# Revit family: Thorn Caelon S30i
name_source: partatom
category: Lighting Fixtures
units: mm (PartAtom-declared; Revit-internal decimal feet)

## family parameters
Cut with Voids When Loaded = No
Host = Face
Light Source = No
Maintain Annotation Orientation = No
Part Type = Normal
Room Calculation Point = No
Round Connector Dimension = Use Diameter
Shared = No

## types (193) — shared parameters
Apparent Load = 20 VA
Assembly Code = Pr_70_70_48_75
Description = Outdoor flood and spotlight luminaires
Export Type to IFC As = IfcLightFixtureType
Has Cowl = No
Has Ground Spike = No
Lamp = LED
Luminaire Height = 210 mm  [stored 0.688976 ft]
Luminaire Length = 160 mm  [stored 0.524934 ft]
Luminaire Width = 149 mm  [stored 0.488845 ft]
Manufacturer = Thorn Lighting
Power Factor = 1
Type Accessory Cowl Black = Thorn CAELON-Accessory-S12i_S20i_S30i : CAELON S COWL/BK
Type Accessory Cowl White = Thorn CAELON-Accessory-S12i_S20i_S30i : CAELON S COWL/WH
Type Accessory Ground Spike Black = Thorn CAELON-Accessory-S12i_S20i_S30i : CAELON S12/20/30 GROUND SPIKE
Type Bracket Black = Thorn-Parts-CAELON-Bracket-S12l : Black
Type Bracket White = Thorn-Parts-CAELON-Bracket-S12l : White
Type Housing Black = Thorn-Parts-CAELON-Housing-S12l : Black
Type Housing White = Thorn-Parts-CAELON-Housing-S12l : White
Type IFC Predefined Type = DIRECTIONSOURCE
URL = https://www.thornlighting.com
zero-valued in all types: Default Elevation

## per-type parameters (varying)
| type | Housing Finish Black | Housing Finish White | Model | Optic | Type Accessory Cowl | Type Bracket | Type Housing | Type Image | Type Light Source |
| CAELON S30i 3000-827 5D WH 66 BC | No | Yes | 21034300 | - | Thorn CAELON-Accessory-S12i_S20i_S30i : CAELON S COWL/WH | Thorn-Parts-CAELON-Bracket-S12l : White | Thorn-Parts-CAELON-Housing-S12l : White | TLG_CAEL_F_S12i-S20i-S30i_WH.png | Thorn-Light Sources-CAELON S30i : CAELON S30i 3000-827 5D WH 66 BC_photometric_data |
| CAELON S30i 3000-827 M BK 66 BC | Yes | No | 21035660 | Medium | Thorn CAELON-Accessory-S12i_S20i_S30i : CAELON S COWL/BK | Thorn-Parts-CAELON-Bracket-S12l : Black | Thorn-Parts-CAELON-Housing-S12l : Black | TLG_CAEL_F_S12i-S20i-S30i_BK.png | Thorn-Light Sources-CAELON S30i : CAELON S30i 3000-827 M BK 66 BC_photometric_data |
| CAELON S30I 3000-827 M BK 66 HF | Yes | No | 21035658 | Medium | Thorn CAELON-Accessory-S12i_S20i_S30i : CAELON S COWL/BK | Thorn-Parts-CAELON-Bracket-S12l : Black | Thorn-Parts-CAELON-Housing-S12l : Black | TLG_CAEL_F_S12i-S20i-S30i_BK.png | Thorn-Light Sources-CAELON S30i : CAELON S30I 3000-827 M BK 66 HF_photometric_data |
| CAELON S30I 3000-827 M BK 66 HFX | Yes | No | 21035659 | Medium | Thorn CAELON-Accessory-S12i_S20i_S30i : CAELON S COWL/BK | Thorn-Parts-CAELON-Bracket-S12l : Black | Thorn-Parts-CAELON-Housing-S12l : Black | TLG_CAEL_F_S12i-S20i-S30i_BK.png | Thorn-Light Sources-CAELON S30i : CAELON S30I 3000-827 M BK 66 HFX_photometric_data |
| CAELON S30i 3000-827 M BK HL 66 BC | Yes | No | 21035657 | Medium | Thorn CAELON-Accessory-S12i_S20i_S30i : CAELON S COWL/BK | Thorn-Parts-CAELON-Bracket-S12l : Black | Thorn-Parts-CAELON-Housing-S12l : Black | TLG_CAEL_F_S12i-S20i-S30i_BK.png | Thorn-Light Sources-CAELON S30i : CAELON S30i 3000-827 M BK HL 66 BC_photometric_data |
| CAELON S30I 3000-827 M BK HL 66 HF | Yes | No | 21035655 | Medium | Thorn CAELON-Accessory-S12i_S20i_S30i : CAELON S COWL/BK | Thorn-Parts-CAELON-Bracket-S12l : Black | Thorn-Parts-CAELON-Housing-S12l : Black | TLG_CAEL_F_S12i-S20i-S30i_BK.png | Thorn-Light Sources-CAELON S30i : CAELON S30I 3000-827 M BK HL 66 HF_photometric_data |
| CAELON S30I 3000-827 M BK HL 66 HFX | Yes | No | 21035656 | Medium | Thorn CAELON-Accessory-S12i_S20i_S30i : CAELON S COWL/BK | Thorn-Parts-CAELON-Bracket-S12l : Black | Thorn-Parts-CAELON-Housing-S12l : Black | TLG_CAEL_F_S12i-S20i-S30i_BK.png | Thorn-Light Sources-CAELON S30i : CAELON S30I 3000-827 M BK HL 66 HFX_photometric_data |
| CAELON S30i 3000-827 M WH 66 BC | No | Yes | 21035666 | Medium | Thorn CAELON-Accessory-S12i_S20i_S30i : CAELON S COWL/WH | Thorn-Parts-CAELON-Bracket-S12l : White | Thorn-Parts-CAELON-Housing-S12l : White | TLG_CAEL_F_S12i-S20i-S30i_WH.png | Thorn-Light Sources-CAELON S30i : CAELON S30i 3000-827 M WH 66 BC_photometric_data |
| CAELON S30I 3000-827 M WH 66 HF | No | Yes | 21035664 | Medium | Thorn CAELON-Accessory-S12i_S20i_S30i : CAELON S COWL/WH | Thorn-Parts-CAELON-Bracket-S12l : White | Thorn-Parts-CAELON-Housing-S12l : White | TLG_CAEL_F_S12i-S20i-S30i_WH.png | Thorn-Light Sources-CAELON S30i : CAELON S30I 3000-827 M WH 66 HF_photometric_data |
| CAELON S30I 3000-827 M WH 66 HFX | No | Yes | 21035665 | Medium | Thorn CAELON-Accessory-S12i_S20i_S30i : CAELON S COWL/WH | Thorn-Parts-CAELON-Bracket-S12l : White | Thorn-Parts-CAELON-Housing-S12l : White | TLG_CAEL_F_S12i-S20i-S30i_WH.png | Thorn-Light Sources-CAELON S30i : CAELON S30I 3000-827 M WH 66 HFX_photometric_data |
| CAELON S30i 3000-827 M WH HL 66 BC | No | Yes | 21035663 | Medium | Thorn CAELON-Accessory-S12i_S20i_S30i : CAELON S COWL/WH | Thorn-Parts-CAELON-Bracket-S12l : White | Thorn-Parts-CAELON-Housing-S12l : White | TLG_CAEL_F_S12i-S20i-S30i_WH.png | Thorn-Light Sources-CAELON S30i : CAELON S30i 3000-827 M WH HL 66 BC_photometric_data |
| CAELON S30I 3000-827 M WH HL 66 HF | No | Yes | 21035661 | Medium | Thorn CAELON-Accessory-S12i_S20i_S30i : CAELON S COWL/WH | Thorn-Parts-CAELON-Bracket-S12l : White | Thorn-Parts-CAELON-Housing-S12l : White | TLG_CAEL_F_S12i-S20i-S30i_WH.png | Thorn-Light Sources-CAELON S30i : CAELON S30I 3000-827 M WH HL 66 HF_photometric_data |
| CAELON S30I 3000-827 M WH HL 66 HFX | No | Yes | 21035662 | Medium | Thorn CAELON-Accessory-S12i_S20i_S30i : CAELON S COWL/WH | Thorn-Parts-CAELON-Bracket-S12l : White | Thorn-Parts-CAELON-Housing-S12l : White | TLG_CAEL_F_S12i-S20i-S30i_WH.png | Thorn-Light Sources-CAELON S30i : CAELON S30I 3000-827 M WH HL 66 HFX_photometric_data |
| CAELON S30i 3000-827 N BK 66 BC | Yes | No | 21034286 | Narrow | Thorn CAELON-Accessory-S12i_S20i_S30i : CAELON S COWL/BK | Thorn-Parts-CAELON-Bracket-S12l : Black | Thorn-Parts-CAELON-Housing-S12l : Black | TLG_CAEL_F_S12i-S20i-S30i_BK.png | Thorn-Light Sources-CAELON S30i : CAELON S30i 3000-827 N BK 66 BC_photometric_data |
| CAELON S30I 3000-827 N BK 66 HF | Yes | No | 21034284 | Narrow | Thorn CAELON-Accessory-S12i_S20i_S30i : CAELON S COWL/BK | Thorn-Parts-CAELON-Bracket-S12l : Black | Thorn-Parts-CAELON-Housing-S12l : Black | TLG_CAEL_F_S12i-S20i-S30i_BK.png | Thorn-Light Sources-CAELON S30i : CAELON S30I 3000-827 N BK 66 HF_photometric_data |
| CAELON S30I 3000-827 N BK 66 HFX | Yes | No | 21034285 | Narrow | Thorn CAELON-Accessory-S12i_S20i_S30i : CAELON S COWL/BK | Thorn-Parts-CAELON-Bracket-S12l : Black | Thorn-Parts-CAELON-Housing-S12l : Black | TLG_CAEL_F_S12i-S20i-S30i_BK.png | Thorn-Light Sources-CAELON S30i : CAELON S30I 3000-827 N BK 66 HFX_photometric_data |
| CAELON S30i 3000-827 N BK HL 66 BC | Yes | No | 21034283 | Narrow | Thorn CAELON-Accessory-S12i_S20i_S30i : CAELON S COWL/BK | Thorn-Parts-CAELON-Bracket-S12l : Black | Thorn-Parts-CAELON-Housing-S12l : Black | TLG_CAEL_F_S12i-S20i-S30i_BK.png | Thorn-Light Sources-CAELON S30i : CAELON S30i 3000-827 N BK HL 66 BC_photometric_data |
| CAELON S30I 3000-827 N BK HL 66 HF | Yes | No | 21034281 | Narrow | Thorn CAELON-Accessory-S12i_S20i_S30i : CAELON S COWL/BK | Thorn-Parts-CAELON-Bracket-S12l : Black | Thorn-Parts-CAELON-Housing-S12l : Black | TLG_CAEL_F_S12i-S20i-S30i_BK.png | Thorn-Light Sources-CAELON S30i : CAELON S30I 3000-827 N BK HL 66 HF_photometric_data |
| CAELON S30I 3000-827 N BK HL 66 HFX | Yes | No | 21034282 | Narrow | Thorn CAELON-Accessory-S12i_S20i_S30i : CAELON S COWL/BK | Thorn-Parts-CAELON-Bracket-S12l : Black | Thorn-Parts-CAELON-Housing-S12l : Black | TLG_CAEL_F_S12i-S20i-S30i_BK.png | Thorn-Light Sources-CAELON S30i : CAELON S30I 3000-827 N BK HL 66 HFX_photometric_data |
| CAELON S30i 3000-827 N WH 66 BC | No | Yes | 21034292 | Narrow | Thorn CAELON-Accessory-S12i_S20i_S30i : CAELON S COWL/WH | Thorn-Parts-CAELON-Bracket-S12l : White | Thorn-Parts-CAELON-Housing-S12l : White | TLG_CAEL_F_S12i-S20i-S30i_WH.png | Thorn-Light Sources-CAELON S30i : CAELON S30i 3000-827 N WH 66 BC_photometric_data |
| CAELON S30I 3000-827 N WH 66 HF | No | Yes | 21034290 | Narrow | Thorn CAELON-Accessory-S12i_S20i_S30i : CAELON S COWL/WH | Thorn-Parts-CAELON-Bracket-S12l : White | Thorn-Parts-CAELON-Housing-S12l : White | TLG_CAEL_F_S12i-S20i-S30i_WH.png | Thorn-Light Sources-CAELON S30i : CAELON S30I 3000-827 N WH 66 HF_photometric_data |
| CAELON S30I 3000-827 N WH 66 HFX | No | Yes | 21034291 | Narrow | Thorn CAELON-Accessory-S12i_S20i_S30i : CAELON S COWL/WH | Thorn-Parts-CAELON-Bracket-S12l : White | Thorn-Parts-CAELON-Housing-S12l : White | TLG_CAEL_F_S12i-S20i-S30i_WH.png | Thorn-Light Sources-CAELON S30i : CAELON S30I 3000-827 N WH 66 HFX_photometric_data |
| CAELON S30i 3000-827 N WH HL 66 BC | No | Yes | 21034289 | Narrow | Thorn CAELON-Accessory-S12i_S20i_S30i : CAELON S COWL/WH | Thorn-Parts-CAELON-Bracket-S12l : White | Thorn-Parts-CAELON-Housing-S12l : White | TLG_CAEL_F_S12i-S20i-S30i_WH.png | Thorn-Light Sources-CAELON S30i : CAELON S30i 3000-827 N WH HL 66 BC_photometric_data |
| CAELON S30I 3000-827 N WH HL 66 HF | No | Yes | 21034287 | Narrow | Thorn CAELON-Accessory-S12i_S20i_S30i : CAELON S COWL/WH | Thorn-Parts-CAELON-Bracket-S12l : White | Thorn-Parts-CAELON-Housing-S12l : White | TLG_CAEL_F_S12i-S20i-S30i_WH.png | Thorn-Light Sources-CAELON S30i : CAELON S30I 3000-827 N WH HL 66 HF_photometric_data |
| CAELON S30I 3000-827 N WH HL 66 HFX | No | Yes | 21034288 | Narrow | Thorn CAELON-Accessory-S12i_S20i_S30i : CAELON S COWL/WH | Thorn-Parts-CAELON-Bracket-S12l : White | Thorn-Parts-CAELON-Housing-S12l : White | TLG_CAEL_F_S12i-S20i-S30i_WH.png | Thorn-Light Sources-CAELON S30i : CAELON S30I 3000-827 N WH HL 66 HFX_photometric_data |
| CAELON S30i 3000-827 SN BK 66 BC | Yes | No | 21034274 | Super Narrow | Thorn CAELON-Accessory-S12i_S20i_S30i : CAELON S COWL/BK | Thorn-Parts-CAELON-Bracket-S12l : Black | Thorn-Parts-CAELON-Housing-S12l : Black | TLG_CAEL_F_S12i-S20i-S30i_BK.png | Thorn-Light Sources-CAELON S30i : CAELON S30i 3000-827 SN BK 66 BC_photometric_data |
| CAELON S30I 3000-827 SN BK 66 HF | Yes | No | 21034272 | Super Narrow | Thorn CAELON-Accessory-S12i_S20i_S30i : CAELON S COWL/BK | Thorn-Parts-CAELON-Bracket-S12l : Black | Thorn-Parts-CAELON-Housing-S12l : Black | TLG_CAEL_F_S12i-S20i-S30i_BK.png | Thorn-Light Sources-CAELON S30i : CAELON S30I 3000-827 SN BK 66 HF_photometric_data |
| CAELON S30I 3000-827 SN BK 66 HFX | Yes | No | 21034273 | Super Narrow | Thorn CAELON-Accessory-S12i_S20i_S30i : CAELON S COWL/BK | Thorn-Parts-CAELON-Bracket-S12l : Black | Thorn-Parts-CAELON-Housing-S12l : Black | TLG_CAEL_F_S12i-S20i-S30i_BK.png | Thorn-Light Sources-CAELON S30i : CAELON S30I 3000-827 SN BK 66 HFX_photometric_data |
| CAELON S30i 3000-827 SN BK HL 66 BC | Yes | No | 21034271 | Super Narrow | Thorn CAELON-Accessory-S12i_S20i_S30i : CAELON S COWL/BK | Thorn-Parts-CAELON-Bracket-S12l : Black | Thorn-Parts-CAELON-Housing-S12l : Black | TLG_CAEL_F_S12i-S20i-S30i_BK.png | Thorn-Light Sources-CAELON S30i : CAELON S30i 3000-827 SN BK HL 66 BC_photometric_data |
| CAELON S30I 3000-827 SN BK HL 66 HF | Yes | No | 21034269 | Super Narrow | Thorn CAELON-Accessory-S12i_S20i_S30i : CAELON S COWL/BK | Thorn-Parts-CAELON-Bracket-S12l : Black | Thorn-Parts-CAELON-Housing-S12l : Black | TLG_CAEL_F_S12i-S20i-S30i_BK.png | Thorn-Light Sources-CAELON S30i : CAELON S30I 3000-827 SN BK HL 66 HF_photometric_data |
| CAELON S30I 3000-827 SN BK HL 66 HFX | Yes | No | 21034270 | Super Narrow | Thorn CAELON-Accessory-S12i_S20i_S30i : CAELON S COWL/BK | Thorn-Parts-CAELON-Bracket-S12l : Black | Thorn-Parts-CAELON-Housing-S12l : Black | TLG_CAEL_F_S12i-S20i-S30i_BK.png | Thorn-Light Sources-CAELON S30i : CAELON S30I 3000-827 SN BK HL 66 HFX_photometric_data |
| CAELON S30i 3000-827 SN WH 66 BC | No | Yes | 21034280 | Super Narrow | Thorn CAELON-Accessory-S12i_S20i_S30i : CAELON S COWL/WH | Thorn-Parts-CAELON-Bracket-S12l : White | Thorn-Parts-CAELON-Housing-S12l : White | TLG_CAEL_F_S12i-S20i-S30i_WH.png | Thorn-Light Sources-CAELON S30i : CAELON S30i 3000-827 SN WH 66 BC_photometric_data |
| CAELON S30I 3000-827 SN WH 66 HF | No | Yes | 21034278 | Super Narrow | Thorn CAELON-Accessory-S12i_S20i_S30i : CAELON S COWL/WH | Thorn-Parts-CAELON-Bracket-S12l : White | Thorn-Parts-CAELON-Housing-S12l : White | TLG_CAEL_F_S12i-S20i-S30i_WH.png | Thorn-Light Sources-CAELON S30i : CAELON S30I 3000-827 SN WH 66 HF_photometric_data |
| CAELON S30I 3000-827 SN WH 66 HFX | No | Yes | 21034279 | Super Narrow | Thorn CAELON-Accessory-S12i_S20i_S30i : CAELON S COWL/WH | Thorn-Parts-CAELON-Bracket-S12l : White | Thorn-Parts-CAELON-Housing-S12l : White | TLG_CAEL_F_S12i-S20i-S30i_WH.png | Thorn-Light Sources-CAELON S30i : CAELON S30I 3000-827 SN WH 66 HFX_photometric_data |
| CAELON S30i 3000-827 SN WH HL 66 BC | No | Yes | 21034277 | Super Narrow | Thorn CAELON-Accessory-S12i_S20i_S30i : CAELON S COWL/WH | Thorn-Parts-CAELON-Bracket-S12l : White | Thorn-Parts-CAELON-Housing-S12l : White | TLG_CAEL_F_S12i-S20i-S30i_WH.png | Thorn-Light Sources-CAELON S30i : CAELON S30i 3000-827 SN WH HL 66 BC_photometric_data |
| CAELON S30I 3000-827 SN WH HL 66 HF | No | Yes | 21034275 | Super Narrow | Thorn CAELON-Accessory-S12i_S20i_S30i : CAELON S COWL/WH | Thorn-Parts-CAELON-Bracket-S12l : White | Thorn-Parts-CAELON-Housing-S12l : White | TLG_CAEL_F_S12i-S20i-S30i_WH.png | Thorn-Light Sources-CAELON S30i : CAELON S30I 3000-827 SN WH HL 66 HF_photometric_data |
| CAELON S30I 3000-827 SN WH HL 66 HFX | No | Yes | 21034276 | Super Narrow | Thorn CAELON-Accessory-S12i_S20i_S30i : CAELON S COWL/WH | Thorn-Parts-CAELON-Bracket-S12l : White | Thorn-Parts-CAELON-Housing-S12l : White | TLG_CAEL_F_S12i-S20i-S30i_WH.png | Thorn-Light Sources-CAELON S30i : CAELON S30I 3000-827 SN WH HL 66 HFX_photometric_data |
| CAELON S30i 3000-827 W BK 66 BC | Yes | No | 21034295 | Wide | Thorn CAELON-Accessory-S12i_S20i_S30i : CAELON S COWL/BK | Thorn-Parts-CAELON-Bracket-S12l : Black | Thorn-Parts-CAELON-Housing-S12l : Black | TLG_CAEL_F_S12i-S20i-S30i_BK.png | Thorn-Light Sources-CAELON S30i : CAELON S30i 3000-827 W BK 66 BC_photometric_data |
| CAELON S30I 3000-827 W BK 66 HF | Yes | No | 21034293 | Wide | Thorn CAELON-Accessory-S12i_S20i_S30i : CAELON S COWL/BK | Thorn-Parts-CAELON-Bracket-S12l : Black | Thorn-Parts-CAELON-Housing-S12l : Black | TLG_CAEL_F_S12i-S20i-S30i_BK.png | Thorn-Light Sources-CAELON S30i : CAELON S30I 3000-827 W BK 66 HF_photometric_data |
| CAELON S30I 3000-827 W BK 66 HFX | Yes | No | 21034294 | Wide | Thorn CAELON-Accessory-S12i_S20i_S30i : CAELON S COWL/BK | Thorn-Parts-CAELON-Bracket-S12l : Black | Thorn-Parts-CAELON-Housing-S12l : Black | TLG_CAEL_F_S12i-S20i-S30i_BK.png | Thorn-Light Sources-CAELON S30i : CAELON S30I 3000-827 W BK 66 HFX_photometric_data |
| CAELON S30i 3000-827 W WH 66 BC | No | Yes | 21034298 | Wide | Thorn CAELON-Accessory-S12i_S20i_S30i : CAELON S COWL/WH | Thorn-Parts-CAELON-Bracket-S12l : White | Thorn-Parts-CAELON-Housing-S12l : White | TLG_CAEL_F_S12i-S20i-S30i_WH.png | Thorn-Light Sources-CAELON S30i : CAELON S30i 3000-827 W WH 66 BC_photometric_data |
| CAELON S30I 3000-827 W WH 66 HF | No | Yes | 21034296 | Wide | Thorn CAELON-Accessory-S12i_S20i_S30i : CAELON S COWL/WH | Thorn-Parts-CAELON-Bracket-S12l : White | Thorn-Parts-CAELON-Housing-S12l : White | TLG_CAEL_F_S12i-S20i-S30i_WH.png | Thorn-Light Sources-CAELON S30i : CAELON S30I 3000-827 W WH 66 HF_photometric_data |
| CAELON S30I 3000-827 W WH 66 HFX | No | Yes | 21034297 | Wide | Thorn CAELON-Accessory-S12i_S20i_S30i : CAELON S COWL/WH | Thorn-Parts-CAELON-Bracket-S12l : White | Thorn-Parts-CAELON-Housing-S12l : White | TLG_CAEL_F_S12i-S20i-S30i_WH.png | Thorn-Light Sources-CAELON S30i : CAELON S30I 3000-827 W WH 66 HFX_photometric_data |
| CAELON S30i 3000-830 5D BK 66 BC | Yes | No | 21034331 |  | Thorn CAELON-Accessory-S12i_S20i_S30i : CAELON S COWL/BK | Thorn-Parts-CAELON-Bracket-S12l : Black | Thorn-Parts-CAELON-Housing-S12l : Black | TLG_CAEL_F_S12i-S20i-S30i_BK.png | Thorn-Light Sources-CAELON S30i : CAELON S30i 3000-830 5D BK 66 BC_photometric_data |
| CAELON S30i 3000-830 5D WH 66 BC | No | Yes | 21034332 |  | Thorn CAELON-Accessory-S12i_S20i_S30i : CAELON S COWL/WH | Thorn-Parts-CAELON-Bracket-S12l : White | Thorn-Parts-CAELON-Housing-S12l : White | TLG_CAEL_F_S12i-S20i-S30i_WH.png | Thorn-Light Sources-CAELON S30i : CAELON S30i 3000-830 5D WH 66 BC_photometric_data |
| CAELON S30i 3000-830 M BK 66 BC | Yes | No | 21035672 | Medium | Thorn CAELON-Accessory-S12i_S20i_S30i : CAELON S COWL/BK | Thorn-Parts-CAELON-Bracket-S12l : Black | Thorn-Parts-CAELON-Housing-S12l : Black | TLG_CAEL_F_S12i-S20i-S30i_BK.png | Thorn-Light Sources-CAELON S30i : CAELON S30i 3000-830 M BK 66 BC_photometric_data |
| CAELON S30I 3000-830 M BK 66 HF | Yes | No | 21035670 | Medium | Thorn CAELON-Accessory-S12i_S20i_S30i : CAELON S COWL/BK | Thorn-Parts-CAELON-Bracket-S12l : Black | Thorn-Parts-CAELON-Housing-S12l : Black | TLG_CAEL_F_S12i-S20i-S30i_BK.png | Thorn-Light Sources-CAELON S30i : CAELON S30I 3000-830 M BK 66 HF_photometric_data |
| CAELON S30I 3000-830 M BK 66 HFX | Yes | No | 21035671 | Medium | Thorn CAELON-Accessory-S12i_S20i_S30i : CAELON S COWL/BK | Thorn-Parts-CAELON-Bracket-S12l : Black | Thorn-Parts-CAELON-Housing-S12l : Black | TLG_CAEL_F_S12i-S20i-S30i_BK.png | Thorn-Light Sources-CAELON S30i : CAELON S30I 3000-830 M BK 66 HFX_photometric_data |
| CAELON S30i 3000-830 M BK HL 66 BC | Yes | No | 21035669 | Medium | Thorn CAELON-Accessory-S12i_S20i_S30i : CAELON S COWL/BK | Thorn-Parts-CAELON-Bracket-S12l : Black | Thorn-Parts-CAELON-Housing-S12l : Black | TLG_CAEL_F_S12i-S20i-S30i_BK.png | Thorn-Light Sources-CAELON S30i : CAELON S30i 3000-830 M BK HL 66 BC_photometric_data |
| CAELON S30I 3000-830 M BK HL 66 HF | Yes | No | 21035667 | Medium | Thorn CAELON-Accessory-S12i_S20i_S30i : CAELON S COWL/BK | Thorn-Parts-CAELON-Bracket-S12l : Black | Thorn-Parts-CAELON-Housing-S12l : Black | TLG_CAEL_F_S12i-S20i-S30i_BK.png | Thorn-Light Sources-CAELON S30i : CAELON S30I 3000-830 M BK HL 66 HF_photometric_data |
| CAELON S30I 3000-830 M BK HL 66 HFX | Yes | No | 21035668 | Medium | Thorn CAELON-Accessory-S12i_S20i_S30i : CAELON S COWL/BK | Thorn-Parts-CAELON-Bracket-S12l : Black | Thorn-Parts-CAELON-Housing-S12l : Black | TLG_CAEL_F_S12i-S20i-S30i_BK.png | Thorn-Light Sources-CAELON S30i : CAELON S30I 3000-830 M BK HL 66 HFX_photometric_data |
| CAELON S30i 3000-830 M WH 66 BC | No | Yes | 21035678 | Medium | Thorn CAELON-Accessory-S12i_S20i_S30i : CAELON S COWL/WH | Thorn-Parts-CAELON-Bracket-S12l : White | Thorn-Parts-CAELON-Housing-S12l : White | TLG_CAEL_F_S12i-S20i-S30i_WH.png | Thorn-Light Sources-CAELON S30i : CAELON S30i 3000-830 M WH 66 BC_photometric_data |
| CAELON S30I 3000-830 M WH 66 HF | No | Yes | 21035676 | Medium | Thorn CAELON-Accessory-S12i_S20i_S30i : CAELON S COWL/WH | Thorn-Parts-CAELON-Bracket-S12l : White | Thorn-Parts-CAELON-Housing-S12l : White | TLG_CAEL_F_S12i-S20i-S30i_WH.png | Thorn-Light Sources-CAELON S30i : CAELON S30I 3000-830 M WH 66 HF_photometric_data |
| CAELON S30I 3000-830 M WH 66 HFX | No | Yes | 21035677 | Medium | Thorn CAELON-Accessory-S12i_S20i_S30i : CAELON S COWL/WH | Thorn-Parts-CAELON-Bracket-S12l : White | Thorn-Parts-CAELON-Housing-S12l : White | TLG_CAEL_F_S12i-S20i-S30i_WH.png | Thorn-Light Sources-CAELON S30i : CAELON S30I 3000-830 M WH 66 HFX_photometric_data |
| CAELON S30i 3000-830 M WH HL 66 BC | No | Yes | 21035675 | Medium | Thorn CAELON-Accessory-S12i_S20i_S30i : CAELON S COWL/WH | Thorn-Parts-CAELON-Bracket-S12l : White | Thorn-Parts-CAELON-Housing-S12l : White | TLG_CAEL_F_S12i-S20i-S30i_WH.png | Thorn-Light Sources-CAELON S30i : CAELON S30i 3000-830 M WH HL 66 BC_photometric_data |
| CAELON S30I 3000-830 M WH HL 66 HF | No | Yes | 21035673 | Medium | Thorn CAELON-Accessory-S12i_S20i_S30i : CAELON S COWL/WH | Thorn-Parts-CAELON-Bracket-S12l : White | Thorn-Parts-CAELON-Housing-S12l : White | TLG_CAEL_F_S12i-S20i-S30i_WH.png | Thorn-Light Sources-CAELON S30i : CAELON S30I 3000-830 M WH HL 66 HF_photometric_data |
| CAELON S30I 3000-830 M WH HL 66 HFX | No | Yes | 21035674 | Medium | Thorn CAELON-Accessory-S12i_S20i_S30i : CAELON S COWL/WH | Thorn-Parts-CAELON-Bracket-S12l : White | Thorn-Parts-CAELON-Housing-S12l : White | TLG_CAEL_F_S12i-S20i-S30i_WH.png | Thorn-Light Sources-CAELON S30i : CAELON S30I 3000-830 M WH HL 66 HFX_photometric_data |
| CAELON S30i 3000-830 N BK 66 BC | Yes | No | 21034318 | Narrow | Thorn CAELON-Accessory-S12i_S20i_S30i : CAELON S COWL/BK | Thorn-Parts-CAELON-Bracket-S12l : Black | Thorn-Parts-CAELON-Housing-S12l : Black | TLG_CAEL_F_S12i-S20i-S30i_BK.png | Thorn-Light Sources-CAELON S30i : CAELON S30i 3000-830 N BK 66 BC_photometric_data |
| CAELON S30I 3000-830 N BK 66 HF | Yes | No | 21034316 | Narrow | Thorn CAELON-Accessory-S12i_S20i_S30i : CAELON S COWL/BK | Thorn-Parts-CAELON-Bracket-S12l : Black | Thorn-Parts-CAELON-Housing-S12l : Black | TLG_CAEL_F_S12i-S20i-S30i_BK.png | Thorn-Light Sources-CAELON S30i : CAELON S30I 3000-830 N BK 66 HF_photometric_data |
| CAELON S30I 3000-830 N BK 66 HFX | Yes | No | 21034317 | Narrow | Thorn CAELON-Accessory-S12i_S20i_S30i : CAELON S COWL/BK | Thorn-Parts-CAELON-Bracket-S12l : Black | Thorn-Parts-CAELON-Housing-S12l : Black | TLG_CAEL_F_S12i-S20i-S30i_BK.png | Thorn-Light Sources-CAELON S30i : CAELON S30I 3000-830 N BK 66 HFX_photometric_data |
| CAELON S30i 3000-830 N BK HL 66 BC | Yes | No | 21034315 | Narrow | Thorn CAELON-Accessory-S12i_S20i_S30i : CAELON S COWL/BK | Thorn-Parts-CAELON-Bracket-S12l : Black | Thorn-Parts-CAELON-Housing-S12l : Black | TLG_CAEL_F_S12i-S20i-S30i_BK.png | Thorn-Light Sources-CAELON S30i : CAELON S30i 3000-830 N BK HL 66 BC_photometric_data |
| CAELON S30I 3000-830 N BK HL 66 HF | Yes | No | 21034313 | Narrow | Thorn CAELON-Accessory-S12i_S20i_S30i : CAELON S COWL/BK | Thorn-Parts-CAELON-Bracket-S12l : Black | Thorn-Parts-CAELON-Housing-S12l : Black | TLG_CAEL_F_S12i-S20i-S30i_BK.png | Thorn-Light Sources-CAELON S30i : CAELON S30I 3000-830 N BK HL 66 HF_photometric_data |
| CAELON S30I 3000-830 N BK HL 66 HFX | Yes | No | 21034314 | Narrow | Thorn CAELON-Accessory-S12i_S20i_S30i : CAELON S COWL/BK | Thorn-Parts-CAELON-Bracket-S12l : Black | Thorn-Parts-CAELON-Housing-S12l : Black | TLG_CAEL_F_S12i-S20i-S30i_BK.png | Thorn-Light Sources-CAELON S30i : CAELON S30I 3000-830 N BK HL 66 HFX_photometric_data |
| CAELON S30i 3000-830 N WH 66 BC | No | Yes | 21034324 | Narrow | Thorn CAELON-Accessory-S12i_S20i_S30i : CAELON S COWL/WH | Thorn-Parts-CAELON-Bracket-S12l : White | Thorn-Parts-CAELON-Housing-S12l : White | TLG_CAEL_F_S12i-S20i-S30i_WH.png | Thorn-Light Sources-CAELON S30i : CAELON S30i 3000-830 N WH 66 BC_photometric_data |
| CAELON S30I 3000-830 N WH 66 HF | No | Yes | 21034322 | Narrow | Thorn CAELON-Accessory-S12i_S20i_S30i : CAELON S COWL/WH | Thorn-Parts-CAELON-Bracket-S12l : White | Thorn-Parts-CAELON-Housing-S12l : White | TLG_CAEL_F_S12i-S20i-S30i_WH.png | Thorn-Light Sources-CAELON S30i : CAELON S30I 3000-830 N WH 66 HF_photometric_data |
| CAELON S30I 3000-830 N WH 66 HFX | No | Yes | 21034323 | Narrow | Thorn CAELON-Accessory-S12i_S20i_S30i : CAELON S COWL/WH | Thorn-Parts-CAELON-Bracket-S12l : White | Thorn-Parts-CAELON-Housing-S12l : White | TLG_CAEL_F_S12i-S20i-S30i_WH.png | Thorn-Light Sources-CAELON S30i : CAELON S30I 3000-830 N WH 66 HFX_photometric_data |
| CAELON S30i 3000-830 N WH HL 66 BC | No | Yes | 21034321 | Narrow | Thorn CAELON-Accessory-S12i_S20i_S30i : CAELON S COWL/WH | Thorn-Parts-CAELON-Bracket-S12l : White | Thorn-Parts-CAELON-Housing-S12l : White | TLG_CAEL_F_S12i-S20i-S30i_WH.png | Thorn-Light Sources-CAELON S30i : CAELON S30i 3000-830 N WH HL 66 BC_photometric_data |
| CAELON S30I 3000-830 N WH HL 66 HF | No | Yes | 21034319 | Narrow | Thorn CAELON-Accessory-S12i_S20i_S30i : CAELON S COWL/WH | Thorn-Parts-CAELON-Bracket-S12l : White | Thorn-Parts-CAELON-Housing-S12l : White | TLG_CAEL_F_S12i-S20i-S30i_WH.png | Thorn-Light Sources-CAELON S30i : CAELON S30I 3000-830 N WH HL 66 HF_photometric_data |
| CAELON S30I 3000-830 N WH HL 66 HFX | No | Yes | 21034320 | Narrow | Thorn CAELON-Accessory-S12i_S20i_S30i : CAELON S COWL/WH | Thorn-Parts-CAELON-Bracket-S12l : White | Thorn-Parts-CAELON-Housing-S12l : White | TLG_CAEL_F_S12i-S20i-S30i_WH.png | Thorn-Light Sources-CAELON S30i : CAELON S30I 3000-830 N WH HL 66 HFX_photometric_data |
| CAELON S30i 3000-830 SN BK 66 BC | Yes | No | 21034306 | Super Narrow | Thorn CAELON-Accessory-S12i_S20i_S30i : CAELON S COWL/BK | Thorn-Parts-CAELON-Bracket-S12l : Black | Thorn-Parts-CAELON-Housing-S12l : Black | TLG_CAEL_F_S12i-S20i-S30i_BK.png | Thorn-Light Sources-CAELON S30i : CAELON S30i 3000-830 SN BK 66 BC_photometric_data |
| CAELON S30I 3000-830 SN BK 66 HF | Yes | No | 21034304 | Super Narrow | Thorn CAELON-Accessory-S12i_S20i_S30i : CAELON S COWL/BK | Thorn-Parts-CAELON-Bracket-S12l : Black | Thorn-Parts-CAELON-Housing-S12l : Black | TLG_CAEL_F_S12i-S20i-S30i_BK.png | Thorn-Light Sources-CAELON S30i : CAELON S30I 3000-830 SN BK 66 HF_photometric_data |
| CAELON S30I 3000-830 SN BK 66 HFX | Yes | No | 21034305 | Super Narrow | Thorn CAELON-Accessory-S12i_S20i_S30i : CAELON S COWL/BK | Thorn-Parts-CAELON-Bracket-S12l : Black | Thorn-Parts-CAELON-Housing-S12l : Black | TLG_CAEL_F_S12i-S20i-S30i_BK.png | Thorn-Light Sources-CAELON S30i : CAELON S30I 3000-830 SN BK 66 HFX_photometric_data |
| CAELON S30i 3000-830 SN BK HL 66 BC | Yes | No | 21034303 | Super Narrow | Thorn CAELON-Accessory-S12i_S20i_S30i : CAELON S COWL/BK | Thorn-Parts-CAELON-Bracket-S12l : Black | Thorn-Parts-CAELON-Housing-S12l : Black | TLG_CAEL_F_S12i-S20i-S30i_BK.png | Thorn-Light Sources-CAELON S30i : CAELON S30i 3000-830 SN BK HL 66 BC_photometric_data |
| CAELON S30I 3000-830 SN BK HL 66 HF | Yes | No | 21034301 | Super Narrow | Thorn CAELON-Accessory-S12i_S20i_S30i : CAELON S COWL/BK | Thorn-Parts-CAELON-Bracket-S12l : Black | Thorn-Parts-CAELON-Housing-S12l : Black | TLG_CAEL_F_S12i-S20i-S30i_BK.png | Thorn-Light Sources-CAELON S30i : CAELON S30I 3000-830 SN BK HL 66 HF_photometric_data |
| CAELON S30I 3000-830 SN BK HL 66 HFX | Yes | No | 21034302 | Super Narrow | Thorn CAELON-Accessory-S12i_S20i_S30i : CAELON S COWL/BK | Thorn-Parts-CAELON-Bracket-S12l : Black | Thorn-Parts-CAELON-Housing-S12l : Black | TLG_CAEL_F_S12i-S20i-S30i_BK.png | Thorn-Light Sources-CAELON S30i : CAELON S30I 3000-830 SN BK HL 66 HFX_photometric_data |
| CAELON S30i 3000-830 SN WH 66 BC | No | Yes | 21034312 | Super Narrow | Thorn CAELON-Accessory-S12i_S20i_S30i : CAELON S COWL/WH | Thorn-Parts-CAELON-Bracket-S12l : White | Thorn-Parts-CAELON-Housing-S12l : White | TLG_CAEL_F_S12i-S20i-S30i_WH.png | Thorn-Light Sources-CAELON S30i : CAELON S30i 3000-830 SN WH 66 BC_photometric_data |
| CAELON S30I 3000-830 SN WH 66 HF | No | Yes | 21034310 | Super Narrow | Thorn CAELON-Accessory-S12i_S20i_S30i : CAELON S COWL/WH | Thorn-Parts-CAELON-Bracket-S12l : White | Thorn-Parts-CAELON-Housing-S12l : White | TLG_CAEL_F_S12i-S20i-S30i_WH.png | Thorn-Light Sources-CAELON S30i : CAELON S30I 3000-830 SN WH 66 HF_photometric_data |
| CAELON S30I 3000-830 SN WH 66 HFX | No | Yes | 21034311 | Super Narrow | Thorn CAELON-Accessory-S12i_S20i_S30i : CAELON S COWL/WH | Thorn-Parts-CAELON-Bracket-S12l : White | Thorn-Parts-CAELON-Housing-S12l : White | TLG_CAEL_F_S12i-S20i-S30i_WH.png | Thorn-Light Sources-CAELON S30i : CAELON S30I 3000-830 SN WH 66 HFX_photometric_data |
| CAELON S30i 3000-830 SN WH HL 66 BC | No | Yes | 21034309 | Super Narrow | Thorn CAELON-Accessory-S12i_S20i_S30i : CAELON S COWL/WH | Thorn-Parts-CAELON-Bracket-S12l : White | Thorn-Parts-CAELON-Housing-S12l : White | TLG_CAEL_F_S12i-S20i-S30i_WH.png | Thorn-Light Sources-CAELON S30i : CAELON S30i 3000-830 SN WH HL 66 BC_photometric_data |
| CAELON S30I 3000-830 SN WH HL 66 HF | No | Yes | 21034307 | Super Narrow | Thorn CAELON-Accessory-S12i_S20i_S30i : CAELON S COWL/WH | Thorn-Parts-CAELON-Bracket-S12l : White | Thorn-Parts-CAELON-Housing-S12l : White | TLG_CAEL_F_S12i-S20i-S30i_WH.png | Thorn-Light Sources-CAELON S30i : CAELON S30I 3000-830 SN WH HL 66 HF_photometric_data |
| CAELON S30I 3000-830 SN WH HL 66 HFX | No | Yes | 21034308 | Super Narrow | Thorn CAELON-Accessory-S12i_S20i_S30i : CAELON S COWL/WH | Thorn-Parts-CAELON-Bracket-S12l : White | Thorn-Parts-CAELON-Housing-S12l : White | TLG_CAEL_F_S12i-S20i-S30i_WH.png | Thorn-Light Sources-CAELON S30i : CAELON S30I 3000-830 SN WH HL 66 HFX_photometric_data |
| CAELON S30i 3000-830 W BK 66 BC | Yes | No | 21034327 | Wide | Thorn CAELON-Accessory-S12i_S20i_S30i : CAELON S COWL/BK | Thorn-Parts-CAELON-Bracket-S12l : Black | Thorn-Parts-CAELON-Housing-S12l : Black | TLG_CAEL_F_S12i-S20i-S30i_BK.png | Thorn-Light Sources-CAELON S30i : CAELON S30i 3000-830 W BK 66 BC_photometric_data |
| CAELON S30I 3000-830 W BK 66 HF | Yes | No | 21034325 | Wide | Thorn CAELON-Accessory-S12i_S20i_S30i : CAELON S COWL/BK | Thorn-Parts-CAELON-Bracket-S12l : Black | Thorn-Parts-CAELON-Housing-S12l : Black | TLG_CAEL_F_S12i-S20i-S30i_BK.png | Thorn-Light Sources-CAELON S30i : CAELON S30I 3000-830 W BK 66 HF_photometric_data |
| CAELON S30I 3000-830 W BK 66 HFX | Yes | No | 21034326 | Wide | Thorn CAELON-Accessory-S12i_S20i_S30i : CAELON S COWL/BK | Thorn-Parts-CAELON-Bracket-S12l : Black | Thorn-Parts-CAELON-Housing-S12l : Black | TLG_CAEL_F_S12i-S20i-S30i_BK.png | Thorn-Light Sources-CAELON S30i : CAELON S30I 3000-830 W BK 66 HFX_photometric_data |
| CAELON S30i 3000-830 W WH 66 BC | No | Yes | 21034330 | Wide | Thorn CAELON-Accessory-S12i_S20i_S30i : CAELON S COWL/WH | Thorn-Parts-CAELON-Bracket-S12l : White | Thorn-Parts-CAELON-Housing-S12l : White | TLG_CAEL_F_S12i-S20i-S30i_WH.png | Thorn-Light Sources-CAELON S30i : CAELON S30i 3000-830 W WH 66 BC_photometric_data |
| CAELON S30I 3000-830 W WH 66 HF | No | Yes | 21034328 | Wide | Thorn CAELON-Accessory-S12i_S20i_S30i : CAELON S COWL/WH | Thorn-Parts-CAELON-Bracket-S12l : White | Thorn-Parts-CAELON-Housing-S12l : White | TLG_CAEL_F_S12i-S20i-S30i_WH.png | Thorn-Light Sources-CAELON S30i : CAELON S30I 3000-830 W WH 66 HF_photometric_data |
| CAELON S30I 3000-830 W WH 66 HFX | No | Yes | 21034329 | Wide | Thorn CAELON-Accessory-S12i_S20i_S30i : CAELON S COWL/WH | Thorn-Parts-CAELON-Bracket-S12l : White | Thorn-Parts-CAELON-Housing-S12l : White | TLG_CAEL_F_S12i-S20i-S30i_WH.png | Thorn-Light Sources-CAELON S30i : CAELON S30I 3000-830 W WH 66 HFX_photometric_data |
| CAELON S30i 3000-840 5D BK 66 BC | Yes | No | 21034363 |  | Thorn CAELON-Accessory-S12i_S20i_S30i : CAELON S COWL/BK | Thorn-Parts-CAELON-Bracket-S12l : Black | Thorn-Parts-CAELON-Housing-S12l : Black | TLG_CAEL_F_S12i-S20i-S30i_BK.png | Thorn-Light Sources-CAELON S30i : CAELON S30i 3000-840 5D BK 66 BC_photometric_data |
| CAELON S30i 3000-840 5D WH 66 BC | No | Yes | 21034364 |  | Thorn CAELON-Accessory-S12i_S20i_S30i : CAELON S COWL/WH | Thorn-Parts-CAELON-Bracket-S12l : White | Thorn-Parts-CAELON-Housing-S12l : White | TLG_CAEL_F_S12i-S20i-S30i_WH.png | Thorn-Light Sources-CAELON S30i : CAELON S30i 3000-840 5D WH 66 BC_photometric_data |
| CAELON S30i 3000-840 M BK 66 BC | Yes | No | 21035684 | Medium | Thorn CAELON-Accessory-S12i_S20i_S30i : CAELON S COWL/BK | Thorn-Parts-CAELON-Bracket-S12l : Black | Thorn-Parts-CAELON-Housing-S12l : Black | TLG_CAEL_F_S12i-S20i-S30i_BK.png | Thorn-Light Sources-CAELON S30i : CAELON S30i 3000-840 M BK 66 BC_photometric_data |
| CAELON S30I 3000-840 M BK 66 HF | Yes | No | 21035682 | Medium | Thorn CAELON-Accessory-S12i_S20i_S30i : CAELON S COWL/BK | Thorn-Parts-CAELON-Bracket-S12l : Black | Thorn-Parts-CAELON-Housing-S12l : Black | TLG_CAEL_F_S12i-S20i-S30i_BK.png | Thorn-Light Sources-CAELON S30i : CAELON S30I 3000-840 M BK 66 HF_photometric_data |
| CAELON S30I 3000-840 M BK 66 HFX | Yes | No | 21035683 | Medium | Thorn CAELON-Accessory-S12i_S20i_S30i : CAELON S COWL/BK | Thorn-Parts-CAELON-Bracket-S12l : Black | Thorn-Parts-CAELON-Housing-S12l : Black | TLG_CAEL_F_S12i-S20i-S30i_BK.png | Thorn-Light Sources-CAELON S30i : CAELON S30I 3000-840 M BK 66 HFX_photometric_data |
| CAELON S30i 3000-840 M BK HL 66 BC | Yes | No | 21035681 | Medium | Thorn CAELON-Accessory-S12i_S20i_S30i : CAELON S COWL/BK | Thorn-Parts-CAELON-Bracket-S12l : Black | Thorn-Parts-CAELON-Housing-S12l : Black | TLG_CAEL_F_S12i-S20i-S30i_BK.png | Thorn-Light Sources-CAELON S30i : CAELON S30i 3000-840 M BK HL 66 BC_photometric_data |
| CAELON S30I 3000-840 M BK HL 66 HF | Yes | No | 21035679 | Medium | Thorn CAELON-Accessory-S12i_S20i_S30i : CAELON S COWL/BK | Thorn-Parts-CAELON-Bracket-S12l : Black | Thorn-Parts-CAELON-Housing-S12l : Black | TLG_CAEL_F_S12i-S20i-S30i_BK.png | Thorn-Light Sources-CAELON S30i : CAELON S30I 3000-840 M BK HL 66 HF_photometric_data |
| CAELON S30I 3000-840 M BK HL 66 HFX | Yes | No | 21035680 | Medium | Thorn CAELON-Accessory-S12i_S20i_S30i : CAELON S COWL/BK | Thorn-Parts-CAELON-Bracket-S12l : Black | Thorn-Parts-CAELON-Housing-S12l : Black | TLG_CAEL_F_S12i-S20i-S30i_BK.png | Thorn-Light Sources-CAELON S30i : CAELON S30I 3000-840 M BK HL 66 HFX_photometric_data |
| CAELON S30i 3000-840 M WH 66 BC | No | Yes | 21035690 | Medium | Thorn CAELON-Accessory-S12i_S20i_S30i : CAELON S COWL/WH | Thorn-Parts-CAELON-Bracket-S12l : White | Thorn-Parts-CAELON-Housing-S12l : White | TLG_CAEL_F_S12i-S20i-S30i_WH.png | Thorn-Light Sources-CAELON S30i : CAELON S30i 3000-840 M WH 66 BC_photometric_data |
| CAELON S30I 3000-840 M WH 66 HF | No | Yes | 21035688 | Medium | Thorn CAELON-Accessory-S12i_S20i_S30i : CAELON S COWL/WH | Thorn-Parts-CAELON-Bracket-S12l : White | Thorn-Parts-CAELON-Housing-S12l : White | TLG_CAEL_F_S12i-S20i-S30i_WH.png | Thorn-Light Sources-CAELON S30i : CAELON S30I 3000-840 M WH 66 HF_photometric_data |
| CAELON S30I 3000-840 M WH 66 HFX | No | Yes | 21035689 | Medium | Thorn CAELON-Accessory-S12i_S20i_S30i : CAELON S COWL/WH | Thorn-Parts-CAELON-Bracket-S12l : White | Thorn-Parts-CAELON-Housing-S12l : White | TLG_CAEL_F_S12i-S20i-S30i_WH.png | Thorn-Light Sources-CAELON S30i : CAELON S30I 3000-840 M WH 66 HFX_photometric_data |
| CAELON S30i 3000-840 M WH HL 66 BC | No | Yes | 21035687 | Medium | Thorn CAELON-Accessory-S12i_S20i_S30i : CAELON S COWL/WH | Thorn-Parts-CAELON-Bracket-S12l : White | Thorn-Parts-CAELON-Housing-S12l : White | TLG_CAEL_F_S12i-S20i-S30i_WH.png | Thorn-Light Sources-CAELON S30i : CAELON S30i 3000-840 M WH HL 66 BC_photometric_data |
| CAELON S30I 3000-840 M WH HL 66 HF | No | Yes | 21035685 | Medium | Thorn CAELON-Accessory-S12i_S20i_S30i : CAELON S COWL/WH | Thorn-Parts-CAELON-Bracket-S12l : White | Thorn-Parts-CAELON-Housing-S12l : White | TLG_CAEL_F_S12i-S20i-S30i_WH.png | Thorn-Light Sources-CAELON S30i : CAELON S30I 3000-840 M WH HL 66 HF_photometric_data |
| CAELON S30I 3000-840 M WH HL 66 HFX | No | Yes | 21035686 | Medium | Thorn CAELON-Accessory-S12i_S20i_S30i : CAELON S COWL/WH | Thorn-Parts-CAELON-Bracket-S12l : White | Thorn-Parts-CAELON-Housing-S12l : White | TLG_CAEL_F_S12i-S20i-S30i_WH.png | Thorn-Light Sources-CAELON S30i : CAELON S30I 3000-840 M WH HL 66 HFX_photometric_data |
| CAELON S30i 3000-840 N BK 66 BC | Yes | No | 21034350 | Narrow | Thorn CAELON-Accessory-S12i_S20i_S30i : CAELON S COWL/BK | Thorn-Parts-CAELON-Bracket-S12l : Black | Thorn-Parts-CAELON-Housing-S12l : Black | TLG_CAEL_F_S12i-S20i-S30i_BK.png | Thorn-Light Sources-CAELON S30i : CAELON S30i 3000-840 N BK 66 BC_photometric_data |
| CAELON S30I 3000-840 N BK 66 HF | Yes | No | 21034348 | Narrow | Thorn CAELON-Accessory-S12i_S20i_S30i : CAELON S COWL/BK | Thorn-Parts-CAELON-Bracket-S12l : Black | Thorn-Parts-CAELON-Housing-S12l : Black | TLG_CAEL_F_S12i-S20i-S30i_BK.png | Thorn-Light Sources-CAELON S30i : CAELON S30I 3000-840 N BK 66 HF_photometric_data |
| CAELON S30I 3000-840 N BK 66 HFX | Yes | No | 21034349 | Narrow | Thorn CAELON-Accessory-S12i_S20i_S30i : CAELON S COWL/BK | Thorn-Parts-CAELON-Bracket-S12l : Black | Thorn-Parts-CAELON-Housing-S12l : Black | TLG_CAEL_F_S12i-S20i-S30i_BK.png | Thorn-Light Sources-CAELON S30i : CAELON S30I 3000-840 N BK 66 HFX_photometric_data |
| CAELON S30i 3000-840 N BK HL 66 BC | Yes | No | 21034347 | Narrow | Thorn CAELON-Accessory-S12i_S20i_S30i : CAELON S COWL/BK | Thorn-Parts-CAELON-Bracket-S12l : Black | Thorn-Parts-CAELON-Housing-S12l : Black | TLG_CAEL_F_S12i-S20i-S30i_BK.png | Thorn-Light Sources-CAELON S30i : CAELON S30i 3000-840 N BK HL 66 BC_photometric_data |
| CAELON S30I 3000-840 N BK HL 66 HF | Yes | No | 21034345 | Narrow | Thorn CAELON-Accessory-S12i_S20i_S30i : CAELON S COWL/BK | Thorn-Parts-CAELON-Bracket-S12l : Black | Thorn-Parts-CAELON-Housing-S12l : Black | TLG_CAEL_F_S12i-S20i-S30i_BK.png | Thorn-Light Sources-CAELON S30i : CAELON S30I 3000-840 N BK HL 66 HF_photometric_data |
| CAELON S30I 3000-840 N BK HL 66 HFX | Yes | No | 21034346 | Narrow | Thorn CAELON-Accessory-S12i_S20i_S30i : CAELON S COWL/BK | Thorn-Parts-CAELON-Bracket-S12l : Black | Thorn-Parts-CAELON-Housing-S12l : Black | TLG_CAEL_F_S12i-S20i-S30i_BK.png | Thorn-Light Sources-CAELON S30i : CAELON S30I 3000-840 N BK HL 66 HFX_photometric_data |
| CAELON S30i 3000-840 N WH 66 BC | No | Yes | 21034356 | Narrow | Thorn CAELON-Accessory-S12i_S20i_S30i : CAELON S COWL/WH | Thorn-Parts-CAELON-Bracket-S12l : White | Thorn-Parts-CAELON-Housing-S12l : White | TLG_CAEL_F_S12i-S20i-S30i_WH.png | Thorn-Light Sources-CAELON S30i : CAELON S30i 3000-840 N WH 66 BC_photometric_data |
| CAELON S30I 3000-840 N WH 66 HF | No | Yes | 21034354 | Narrow | Thorn CAELON-Accessory-S12i_S20i_S30i : CAELON S COWL/WH | Thorn-Parts-CAELON-Bracket-S12l : White | Thorn-Parts-CAELON-Housing-S12l : White | TLG_CAEL_F_S12i-S20i-S30i_WH.png | Thorn-Light Sources-CAELON S30i : CAELON S30I 3000-840 N WH 66 HF_photometric_data |
| CAELON S30I 3000-840 N WH 66 HFX | No | Yes | 21034355 | Narrow | Thorn CAELON-Accessory-S12i_S20i_S30i : CAELON S COWL/WH | Thorn-Parts-CAELON-Bracket-S12l : White | Thorn-Parts-CAELON-Housing-S12l : White | TLG_CAEL_F_S12i-S20i-S30i_WH.png | Thorn-Light Sources-CAELON S30i : CAELON S30I 3000-840 N WH 66 HFX_photometric_data |
| CAELON S30i 3000-840 N WH HL 66 BC | No | Yes | 21034353 | Narrow | Thorn CAELON-Accessory-S12i_S20i_S30i : CAELON S COWL/WH | Thorn-Parts-CAELON-Bracket-S12l : White | Thorn-Parts-CAELON-Housing-S12l : White | TLG_CAEL_F_S12i-S20i-S30i_WH.png | Thorn-Light Sources-CAELON S30i : CAELON S30i 3000-840 N WH HL 66 BC_photometric_data |
| CAELON S30I 3000-840 N WH HL 66 HF | No | Yes | 21034351 | Narrow | Thorn CAELON-Accessory-S12i_S20i_S30i : CAELON S COWL/WH | Thorn-Parts-CAELON-Bracket-S12l : White | Thorn-Parts-CAELON-Housing-S12l : White | TLG_CAEL_F_S12i-S20i-S30i_WH.png | Thorn-Light Sources-CAELON S30i : CAELON S30I 3000-840 N WH HL 66 HF_photometric_data |
| CAELON S30I 3000-840 N WH HL 66 HFX | No | Yes | 21034352 | Narrow | Thorn CAELON-Accessory-S12i_S20i_S30i : CAELON S COWL/WH | Thorn-Parts-CAELON-Bracket-S12l : White | Thorn-Parts-CAELON-Housing-S12l : White | TLG_CAEL_F_S12i-S20i-S30i_WH.png | Thorn-Light Sources-CAELON S30i : CAELON S30I 3000-840 N WH HL 66 HFX_photometric_data |
| CAELON S30i 3000-840 SN BK 66 BC | Yes | No | 21034338 | Super Narrow | Thorn CAELON-Accessory-S12i_S20i_S30i : CAELON S COWL/BK | Thorn-Parts-CAELON-Bracket-S12l : Black | Thorn-Parts-CAELON-Housing-S12l : Black | TLG_CAEL_F_S12i-S20i-S30i_BK.png | Thorn-Light Sources-CAELON S30i : CAELON S30i 3000-840 SN BK 66 BC_photometric_data |
| CAELON S30I 3000-840 SN BK 66 HF | Yes | No | 21034336 | Super Narrow | Thorn CAELON-Accessory-S12i_S20i_S30i : CAELON S COWL/BK | Thorn-Parts-CAELON-Bracket-S12l : Black | Thorn-Parts-CAELON-Housing-S12l : Black | TLG_CAEL_F_S12i-S20i-S30i_BK.png | Thorn-Light Sources-CAELON S30i : CAELON S30I 3000-840 SN BK 66 HF_photometric_data |
| CAELON S30I 3000-840 SN BK 66 HFX | Yes | No | 21034337 | Super Narrow | Thorn CAELON-Accessory-S12i_S20i_S30i : CAELON S COWL/BK | Thorn-Parts-CAELON-Bracket-S12l : Black | Thorn-Parts-CAELON-Housing-S12l : Black | TLG_CAEL_F_S12i-S20i-S30i_BK.png | Thorn-Light Sources-CAELON S30i : CAELON S30I 3000-840 SN BK 66 HFX_photometric_data |
| CAELON S30i 3000-840 SN BK HL 66 BC | Yes | No | 21034335 | Super Narrow | Thorn CAELON-Accessory-S12i_S20i_S30i : CAELON S COWL/BK | Thorn-Parts-CAELON-Bracket-S12l : Black | Thorn-Parts-CAELON-Housing-S12l : Black | TLG_CAEL_F_S12i-S20i-S30i_BK.png | Thorn-Light Sources-CAELON S30i : CAELON S30i 3000-840 SN BK HL 66 BC_photometric_data |
| CAELON S30I 3000-840 SN BK HL 66 HF | Yes | No | 21034333 | Super Narrow | Thorn CAELON-Accessory-S12i_S20i_S30i : CAELON S COWL/BK | Thorn-Parts-CAELON-Bracket-S12l : Black | Thorn-Parts-CAELON-Housing-S12l : Black | TLG_CAEL_F_S12i-S20i-S30i_BK.png | Thorn-Light Sources-CAELON S30i : CAELON S30I 3000-840 SN BK HL 66 HF_photometric_data |
| CAELON S30I 3000-840 SN BK HL 66 HFX | Yes | No | 21034334 | Super Narrow | Thorn CAELON-Accessory-S12i_S20i_S30i : CAELON S COWL/BK | Thorn-Parts-CAELON-Bracket-S12l : Black | Thorn-Parts-CAELON-Housing-S12l : Black | TLG_CAEL_F_S12i-S20i-S30i_BK.png | Thorn-Light Sources-CAELON S30i : CAELON S30I 3000-840 SN BK HL 66 HFX_photometric_data |
| CAELON S30i 3000-840 SN WH 66 BC | No | Yes | 21034344 | Super Narrow | Thorn CAELON-Accessory-S12i_S20i_S30i : CAELON S COWL/WH | Thorn-Parts-CAELON-Bracket-S12l : White | Thorn-Parts-CAELON-Housing-S12l : White | TLG_CAEL_F_S12i-S20i-S30i_WH.png | Thorn-Light Sources-CAELON S30i : CAELON S30i 3000-840 SN WH 66 BC_photometric_data |
| CAELON S30I 3000-840 SN WH 66 HF | No | Yes | 21034342 | Super Narrow | Thorn CAELON-Accessory-S12i_S20i_S30i : CAELON S COWL/WH | Thorn-Parts-CAELON-Bracket-S12l : White | Thorn-Parts-CAELON-Housing-S12l : White | TLG_CAEL_F_S12i-S20i-S30i_WH.png | Thorn-Light Sources-CAELON S30i : CAELON S30I 3000-840 SN WH 66 HF_photometric_data |
| CAELON S30I 3000-840 SN WH 66 HFX | No | Yes | 21034343 | Super Narrow | Thorn CAELON-Accessory-S12i_S20i_S30i : CAELON S COWL/WH | Thorn-Parts-CAELON-Bracket-S12l : White | Thorn-Parts-CAELON-Housing-S12l : White | TLG_CAEL_F_S12i-S20i-S30i_WH.png | Thorn-Light Sources-CAELON S30i : CAELON S30I 3000-840 SN WH 66 HFX_photometric_data |
| CAELON S30i 3000-840 SN WH HL 66 BC | No | Yes | 21034341 | Super Narrow | Thorn CAELON-Accessory-S12i_S20i_S30i : CAELON S COWL/WH | Thorn-Parts-CAELON-Bracket-S12l : White | Thorn-Parts-CAELON-Housing-S12l : White | TLG_CAEL_F_S12i-S20i-S30i_WH.png | Thorn-Light Sources-CAELON S30i : CAELON S30i 3000-840 SN WH HL 66 BC_photometric_data |
| CAELON S30I 3000-840 SN WH HL 66 HF | No | Yes | 21034339 | Super Narrow | Thorn CAELON-Accessory-S12i_S20i_S30i : CAELON S COWL/WH | Thorn-Parts-CAELON-Bracket-S12l : White | Thorn-Parts-CAELON-Housing-S12l : White | TLG_CAEL_F_S12i-S20i-S30i_WH.png | Thorn-Light Sources-CAELON S30i : CAELON S30I 3000-840 SN WH HL 66 HF_photometric_data |
| CAELON S30I 3000-840 SN WH HL 66 HFX | No | Yes | 21034340 | Super Narrow | Thorn CAELON-Accessory-S12i_S20i_S30i : CAELON S COWL/WH | Thorn-Parts-CAELON-Bracket-S12l : White | Thorn-Parts-CAELON-Housing-S12l : White | TLG_CAEL_F_S12i-S20i-S30i_WH.png | Thorn-Light Sources-CAELON S30i : CAELON S30I 3000-840 SN WH HL 66 HFX_photometric_data |
| CAELON S30i 3000-840 W BK 66 BC | Yes | No | 21034359 | Wide | Thorn CAELON-Accessory-S12i_S20i_S30i : CAELON S COWL/BK | Thorn-Parts-CAELON-Bracket-S12l : Black | Thorn-Parts-CAELON-Housing-S12l : Black | TLG_CAEL_F_S12i-S20i-S30i_BK.png | Thorn-Light Sources-CAELON S30i : CAELON S30i 3000-840 W BK 66 BC_photometric_data |
| CAELON S30I 3000-840 W BK 66 HF | Yes | No | 21034357 | Wide | Thorn CAELON-Accessory-S12i_S20i_S30i : CAELON S COWL/BK | Thorn-Parts-CAELON-Bracket-S12l : Black | Thorn-Parts-CAELON-Housing-S12l : Black | TLG_CAEL_F_S12i-S20i-S30i_BK.png | Thorn-Light Sources-CAELON S30i : CAELON S30I 3000-840 W BK 66 HF_photometric_data |
| CAELON S30I 3000-840 W BK 66 HFX | Yes | No | 21034358 | Wide | Thorn CAELON-Accessory-S12i_S20i_S30i : CAELON S COWL/BK | Thorn-Parts-CAELON-Bracket-S12l : Black | Thorn-Parts-CAELON-Housing-S12l : Black | TLG_CAEL_F_S12i-S20i-S30i_BK.png | Thorn-Light Sources-CAELON S30i : CAELON S30I 3000-840 W BK 66 HFX_photometric_data |
| CAELON S30i 3000-840 W WH 66 BC | No | Yes | 21034362 | Wide | Thorn CAELON-Accessory-S12i_S20i_S30i : CAELON S COWL/WH | Thorn-Parts-CAELON-Bracket-S12l : White | Thorn-Parts-CAELON-Housing-S12l : White | TLG_CAEL_F_S12i-S20i-S30i_WH.png | Thorn-Light Sources-CAELON S30i : CAELON S30i 3000-840 W WH 66 BC_photometric_data |
| CAELON S30I 3000-840 W WH 66 HF | No | Yes | 21034360 | Wide | Thorn CAELON-Accessory-S12i_S20i_S30i : CAELON S COWL/WH | Thorn-Parts-CAELON-Bracket-S12l : White | Thorn-Parts-CAELON-Housing-S12l : White | TLG_CAEL_F_S12i-S20i-S30i_WH.png | Thorn-Light Sources-CAELON S30i : CAELON S30I 3000-840 W WH 66 HF_photometric_data |
| CAELON S30I 3000-840 W WH 66 HFX | No | Yes | 21034361 | Wide | Thorn CAELON-Accessory-S12i_S20i_S30i : CAELON S COWL/WH | Thorn-Parts-CAELON-Bracket-S12l : White | Thorn-Parts-CAELON-Housing-S12l : White | TLG_CAEL_F_S12i-S20i-S30i_WH.png | Thorn-Light Sources-CAELON S30i : CAELON S30I 3000-840 W WH 66 HFX_photometric_data |
| CAELON S30i 3000-DW 5D BK 66 BC | Yes | No | 21034385 |  | Thorn CAELON-Accessory-S12i_S20i_S30i : CAELON S COWL/BK | Thorn-Parts-CAELON-Bracket-S12l : Black | Thorn-Parts-CAELON-Housing-S12l : Black | TLG_CAEL_F_S12i-S20i-S30i_BK.png | Thorn-Light Sources-CAELON S30i : CAELON S30i 3000-DW 5D BK 66 BC_photometric_data |
| CAELON S30i 3000-DW 5D WH 66 BC | No | Yes | 21034386 |  | Thorn CAELON-Accessory-S12i_S20i_S30i : CAELON S COWL/WH | Thorn-Parts-CAELON-Bracket-S12l : White | Thorn-Parts-CAELON-Housing-S12l : White | TLG_CAEL_F_S12i-S20i-S30i_WH.png | Thorn-Light Sources-CAELON S30i : CAELON S30i 3000-DW 5D WH 66 BC_photometric_data |
| CAELON S30i 3000-DW M BK 66 BC | Yes | No | 21035694 | Medium | Thorn CAELON-Accessory-S12i_S20i_S30i : CAELON S COWL/BK | Thorn-Parts-CAELON-Bracket-S12l : Black | Thorn-Parts-CAELON-Housing-S12l : Black | TLG_CAEL_F_S12i-S20i-S30i_BK.png | Thorn-Light Sources-CAELON S30i : CAELON S30i 3000-DW M BK 66 BC_photometric_data |
| CAELON S30I 3000-DW M BK 66 HFX | Yes | No | 21035693 | Medium | Thorn CAELON-Accessory-S12i_S20i_S30i : CAELON S COWL/BK | Thorn-Parts-CAELON-Bracket-S12l : Black | Thorn-Parts-CAELON-Housing-S12l : Black | TLG_CAEL_F_S12i-S20i-S30i_BK.png | Thorn-Light Sources-CAELON S30i : CAELON S30I 3000-DW M BK 66 HFX_photometric_data |
| CAELON S30i 3000-DW M BK HL 66 BC | Yes | No | 21035692 | Medium | Thorn CAELON-Accessory-S12i_S20i_S30i : CAELON S COWL/BK | Thorn-Parts-CAELON-Bracket-S12l : Black | Thorn-Parts-CAELON-Housing-S12l : Black | TLG_CAEL_F_S12i-S20i-S30i_BK.png | Thorn-Light Sources-CAELON S30i : CAELON S30i 3000-DW M BK HL 66 BC_photometric_data |
| CAELON S30I 3000-DW M BK HL 66 HFX | Yes | No | 21035691 | Medium | Thorn CAELON-Accessory-S12i_S20i_S30i : CAELON S COWL/BK | Thorn-Parts-CAELON-Bracket-S12l : Black | Thorn-Parts-CAELON-Housing-S12l : Black | TLG_CAEL_F_S12i-S20i-S30i_BK.png | Thorn-Light Sources-CAELON S30i : CAELON S30I 3000-DW M BK HL 66 HFX_photometric_data |
| CAELON S30i 3000-DW M WH 66 BC | No | Yes | 21035698 | Medium | Thorn CAELON-Accessory-S12i_S20i_S30i : CAELON S COWL/WH | Thorn-Parts-CAELON-Bracket-S12l : White | Thorn-Parts-CAELON-Housing-S12l : White | TLG_CAEL_F_S12i-S20i-S30i_WH.png | Thorn-Light Sources-CAELON S30i : CAELON S30i 3000-DW M WH 66 BC_photometric_data |
| CAELON S30I 3000-DW M WH 66 HFX | No | Yes | 21035697 | Medium | Thorn CAELON-Accessory-S12i_S20i_S30i : CAELON S COWL/WH | Thorn-Parts-CAELON-Bracket-S12l : White | Thorn-Parts-CAELON-Housing-S12l : White | TLG_CAEL_F_S12i-S20i-S30i_WH.png | Thorn-Light Sources-CAELON S30i : CAELON S30I 3000-DW M WH 66 HFX_photometric_data |
| CAELON S30i 3000-DW M WH HL 66 BC | No | Yes | 21035696 | Medium | Thorn CAELON-Accessory-S12i_S20i_S30i : CAELON S COWL/WH | Thorn-Parts-CAELON-Bracket-S12l : White | Thorn-Parts-CAELON-Housing-S12l : White | TLG_CAEL_F_S12i-S20i-S30i_WH.png | Thorn-Light Sources-CAELON S30i : CAELON S30i 3000-DW M WH HL 66 BC_photometric_data |
| CAELON S30I 3000-DW M WH HL 66 HFX | No | Yes | 21035695 | Medium | Thorn CAELON-Accessory-S12i_S20i_S30i : CAELON S COWL/WH | Thorn-Parts-CAELON-Bracket-S12l : White | Thorn-Parts-CAELON-Housing-S12l : White | TLG_CAEL_F_S12i-S20i-S30i_WH.png | Thorn-Light Sources-CAELON S30i : CAELON S30I 3000-DW M WH HL 66 HFX_photometric_data |
| CAELON S30i 3000-DW N BK 66 BC | Yes | No | 21034376 | Narrow | Thorn CAELON-Accessory-S12i_S20i_S30i : CAELON S COWL/BK | Thorn-Parts-CAELON-Bracket-S12l : Black | Thorn-Parts-CAELON-Housing-S12l : Black | TLG_CAEL_F_S12i-S20i-S30i_BK.png | Thorn-Light Sources-CAELON S30i : CAELON S30i 3000-DW N BK 66 BC_photometric_data |
| CAELON S30I 3000-DW N BK 66 HFX | Yes | No | 21034375 | Narrow | Thorn CAELON-Accessory-S12i_S20i_S30i : CAELON S COWL/BK | Thorn-Parts-CAELON-Bracket-S12l : Black | Thorn-Parts-CAELON-Housing-S12l : Black | TLG_CAEL_F_S12i-S20i-S30i_BK.png | Thorn-Light Sources-CAELON S30i : CAELON S30I 3000-DW N BK 66 HFX_photometric_data |
| CAELON S30i 3000-DW N BK HL 66 BC | Yes | No | 21034374 | Narrow | Thorn CAELON-Accessory-S12i_S20i_S30i : CAELON S COWL/BK | Thorn-Parts-CAELON-Bracket-S12l : Black | Thorn-Parts-CAELON-Housing-S12l : Black | TLG_CAEL_F_S12i-S20i-S30i_BK.png | Thorn-Light Sources-CAELON S30i : CAELON S30i 3000-DW N BK HL 66 BC_photometric_data |
| CAELON S30I 3000-DW N BK HL 66 HFX | Yes | No | 21034373 | Narrow | Thorn CAELON-Accessory-S12i_S20i_S30i : CAELON S COWL/BK | Thorn-Parts-CAELON-Bracket-S12l : Black | Thorn-Parts-CAELON-Housing-S12l : Black | TLG_CAEL_F_S12i-S20i-S30i_BK.png | Thorn-Light Sources-CAELON S30i : CAELON S30I 3000-DW N BK HL 66 HFX_photometric_data |
| CAELON S30i 3000-DW N WH 66 BC | No | Yes | 21034380 | Narrow | Thorn CAELON-Accessory-S12i_S20i_S30i : CAELON S COWL/WH | Thorn-Parts-CAELON-Bracket-S12l : White | Thorn-Parts-CAELON-Housing-S12l : White | TLG_CAEL_F_S12i-S20i-S30i_WH.png | Thorn-Light Sources-CAELON S30i : CAELON S30i 3000-DW N WH 66 BC_photometric_data |
| CAELON S30I 3000-DW N WH 66 HFX | No | Yes | 21034379 | Narrow | Thorn CAELON-Accessory-S12i_S20i_S30i : CAELON S COWL/WH | Thorn-Parts-CAELON-Bracket-S12l : White | Thorn-Parts-CAELON-Housing-S12l : White | TLG_CAEL_F_S12i-S20i-S30i_WH.png | Thorn-Light Sources-CAELON S30i : CAELON S30I 3000-DW N WH 66 HFX_photometric_data |
| CAELON S30i 3000-DW N WH HL 66 BC | No | Yes | 21034378 | Narrow | Thorn CAELON-Accessory-S12i_S20i_S30i : CAELON S COWL/WH | Thorn-Parts-CAELON-Bracket-S12l : White | Thorn-Parts-CAELON-Housing-S12l : White | TLG_CAEL_F_S12i-S20i-S30i_WH.png | Thorn-Light Sources-CAELON S30i : CAELON S30i 3000-DW N WH HL 66 BC_photometric_data |
| CAELON S30I 3000-DW N WH HL 66 HFX | No | Yes | 21034377 | Narrow | Thorn CAELON-Accessory-S12i_S20i_S30i : CAELON S COWL/WH | Thorn-Parts-CAELON-Bracket-S12l : White | Thorn-Parts-CAELON-Housing-S12l : White | TLG_CAEL_F_S12i-S20i-S30i_WH.png | Thorn-Light Sources-CAELON S30i : CAELON S30I 3000-DW N WH HL 66 HFX_photometric_data |
| CAELON S30i 3000-DW SN BK 66 BC | Yes | No | 21034368 | Super Narrow | Thorn CAELON-Accessory-S12i_S20i_S30i : CAELON S COWL/BK | Thorn-Parts-CAELON-Bracket-S12l : Black | Thorn-Parts-CAELON-Housing-S12l : Black | TLG_CAEL_F_S12i-S20i-S30i_BK.png | Thorn-Light Sources-CAELON S30i : CAELON S30i 3000-DW SN BK 66 BC_photometric_data |
| CAELON S30I 3000-DW SN BK 66 HFX | Yes | No | 21034367 | Super Narrow | Thorn CAELON-Accessory-S12i_S20i_S30i : CAELON S COWL/BK | Thorn-Parts-CAELON-Bracket-S12l : Black | Thorn-Parts-CAELON-Housing-S12l : Black | TLG_CAEL_F_S12i-S20i-S30i_BK.png | Thorn-Light Sources-CAELON S30i : CAELON S30I 3000-DW SN BK 66 HFX_photometric_data |
| CAELON S30i 3000-DW SN BK HL 66 BC | Yes | No | 21034366 | Super Narrow | Thorn CAELON-Accessory-S12i_S20i_S30i : CAELON S COWL/BK | Thorn-Parts-CAELON-Bracket-S12l : Black | Thorn-Parts-CAELON-Housing-S12l : Black | TLG_CAEL_F_S12i-S20i-S30i_BK.png | Thorn-Light Sources-CAELON S30i : CAELON S30i 3000-DW SN BK HL 66 BC_photometric_data |
| CAELON S30I 3000-DW SN BK HL 66 HFX | Yes | No | 21034365 | Super Narrow | Thorn CAELON-Accessory-S12i_S20i_S30i : CAELON S COWL/BK | Thorn-Parts-CAELON-Bracket-S12l : Black | Thorn-Parts-CAELON-Housing-S12l : Black | TLG_CAEL_F_S12i-S20i-S30i_BK.png | Thorn-Light Sources-CAELON S30i : CAELON S30I 3000-DW SN BK HL 66 HFX_photometric_data |
| CAELON S30i 3000-DW SN WH 66 BC | No | Yes | 21034372 | Super Narrow | Thorn CAELON-Accessory-S12i_S20i_S30i : CAELON S COWL/WH | Thorn-Parts-CAELON-Bracket-S12l : White | Thorn-Parts-CAELON-Housing-S12l : White | TLG_CAEL_F_S12i-S20i-S30i_WH.png | Thorn-Light Sources-CAELON S30i : CAELON S30i 3000-DW SN WH 66 BC_photometric_data |
| CAELON S30I 3000-DW SN WH 66 HFX | No | Yes | 21034371 | Super Narrow | Thorn CAELON-Accessory-S12i_S20i_S30i : CAELON S COWL/WH | Thorn-Parts-CAELON-Bracket-S12l : White | Thorn-Parts-CAELON-Housing-S12l : White | TLG_CAEL_F_S12i-S20i-S30i_WH.png | Thorn-Light Sources-CAELON S30i : CAELON S30I 3000-DW SN WH 66 HFX_photometric_data |
| CAELON S30i 3000-DW SN WH HL 66 BC | No | Yes | 21034370 | Super Narrow | Thorn CAELON-Accessory-S12i_S20i_S30i : CAELON S COWL/WH | Thorn-Parts-CAELON-Bracket-S12l : White | Thorn-Parts-CAELON-Housing-S12l : White | TLG_CAEL_F_S12i-S20i-S30i_WH.png | Thorn-Light Sources-CAELON S30i : CAELON S30i 3000-DW SN WH HL 66 BC_photometric_data |
| CAELON S30I 3000-DW SN WH HL 66 HFX | No | Yes | 21034369 | Super Narrow | Thorn CAELON-Accessory-S12i_S20i_S30i : CAELON S COWL/WH | Thorn-Parts-CAELON-Bracket-S12l : White | Thorn-Parts-CAELON-Housing-S12l : White | TLG_CAEL_F_S12i-S20i-S30i_WH.png | Thorn-Light Sources-CAELON S30i : CAELON S30I 3000-DW SN WH HL 66 HFX_photometric_data |
| CAELON S30i 3000-DW W BK 66 BC | Yes | No | 21034382 | Wide | Thorn CAELON-Accessory-S12i_S20i_S30i : CAELON S COWL/BK | Thorn-Parts-CAELON-Bracket-S12l : Black | Thorn-Parts-CAELON-Housing-S12l : Black | TLG_CAEL_F_S12i-S20i-S30i_BK.png | Thorn-Light Sources-CAELON S30i : CAELON S30i 3000-DW W BK 66 BC_photometric_data |
| CAELON S30I 3000-DW W BK 66 HFX | Yes | No | 21034381 | Wide | Thorn CAELON-Accessory-S12i_S20i_S30i : CAELON S COWL/BK | Thorn-Parts-CAELON-Bracket-S12l : Black | Thorn-Parts-CAELON-Housing-S12l : Black | TLG_CAEL_F_S12i-S20i-S30i_BK.png | Thorn-Light Sources-CAELON S30i : CAELON S30I 3000-DW W BK 66 HFX_photometric_data |
| CAELON S30i 3000-DW W WH 66 BC | No | Yes | 21034384 | Wide | Thorn CAELON-Accessory-S12i_S20i_S30i : CAELON S COWL/WH | Thorn-Parts-CAELON-Bracket-S12l : White | Thorn-Parts-CAELON-Housing-S12l : White | TLG_CAEL_F_S12i-S20i-S30i_WH.png | Thorn-Light Sources-CAELON S30i : CAELON S30i 3000-DW W WH 66 BC_photometric_data |
| CAELON S30I 3000-DW W WH 66 HFX | No | Yes | 21034383 | Wide | Thorn CAELON-Accessory-S12i_S20i_S30i : CAELON S COWL/WH | Thorn-Parts-CAELON-Bracket-S12l : White | Thorn-Parts-CAELON-Housing-S12l : White | TLG_CAEL_F_S12i-S20i-S30i_WH.png | Thorn-Light Sources-CAELON S30i : CAELON S30I 3000-DW W WH 66 HFX_photometric_data |
| CAELON S30i 3000-RGBW 5D BK 66 BC | Yes | No | 21034418 |  | Thorn CAELON-Accessory-S12i_S20i_S30i : CAELON S COWL/BK | Thorn-Parts-CAELON-Bracket-S12l : Black | Thorn-Parts-CAELON-Housing-S12l : Black | TLG_CAEL_F_S12i-S20i-S30i_BK.png | Thorn-Light Sources-CAELON S30i : CAELON S30i 3000-RGBW 5D BK 66 BC_photometric_data |
| CAELON S30I 3000-RGBW 5D BK 66 DMX | Yes | No | 21034417 |  | Thorn CAELON-Accessory-S12i_S20i_S30i : CAELON S COWL/BK | Thorn-Parts-CAELON-Bracket-S12l : Black | Thorn-Parts-CAELON-Housing-S12l : Black | TLG_CAEL_F_S12i-S20i-S30i_BK.png | Thorn-Light Sources-CAELON S30i : CAELON S30I 3000-RGBW 5D BK 66 DMX_photometric_data |
| CAELON S30i 3000-RGBW 5D WH 66 BC | No | Yes | 21034420 |  | Thorn CAELON-Accessory-S12i_S20i_S30i : CAELON S COWL/WH | Thorn-Parts-CAELON-Bracket-S12l : White | Thorn-Parts-CAELON-Housing-S12l : White | TLG_CAEL_F_S12i-S20i-S30i_WH.png | Thorn-Light Sources-CAELON S30i : CAELON S30i 3000-RGBW 5D WH 66 BC_photometric_data |
| CAELON S30I 3000-RGBW 5D WH 66 DMX | No | Yes | 21034419 |  | Thorn CAELON-Accessory-S12i_S20i_S30i : CAELON S COWL/WH | Thorn-Parts-CAELON-Bracket-S12l : White | Thorn-Parts-CAELON-Housing-S12l : White | TLG_CAEL_F_S12i-S20i-S30i_WH.png | Thorn-Light Sources-CAELON S30i : CAELON S30I 3000-RGBW 5D WH 66 DMX_photometric_data |
| CAELON S30i 3000-RGBW M BK 66 BC | Yes | No | 21035704 | Medium | Thorn CAELON-Accessory-S12i_S20i_S30i : CAELON S COWL/BK | Thorn-Parts-CAELON-Bracket-S12l : Black | Thorn-Parts-CAELON-Housing-S12l : Black | TLG_CAEL_F_S12i-S20i-S30i_BK.png | Thorn-Light Sources-CAELON S30i : CAELON S30i 3000-RGBW M BK 66 BC_photometric_data |
| CAELON S30I 3000-RGBW M BK 66 DMX | Yes | No | 21035703 | Medium | Thorn CAELON-Accessory-S12i_S20i_S30i : CAELON S COWL/BK | Thorn-Parts-CAELON-Bracket-S12l : Black | Thorn-Parts-CAELON-Housing-S12l : Black | TLG_CAEL_F_S12i-S20i-S30i_BK.png | Thorn-Light Sources-CAELON S30i : CAELON S30I 3000-RGBW M BK 66 DMX_photometric_data |
| CAELON S30i 3000-RGBW M BK HL 66 BC | Yes | No | 21035701 | Medium | Thorn CAELON-Accessory-S12i_S20i_S30i : CAELON S COWL/BK | Thorn-Parts-CAELON-Bracket-S12l : Black | Thorn-Parts-CAELON-Housing-S12l : Black | TLG_CAEL_F_S12i-S20i-S30i_BK.png | Thorn-Light Sources-CAELON S30i : CAELON S30i 3000-RGBW M BK HL 66 BC_photometric_data |
| CAELON S30I 3000-RGBW M BK HL 66 DMX | Yes | No | 21035700 | Medium | Thorn CAELON-Accessory-S12i_S20i_S30i : CAELON S COWL/BK | Thorn-Parts-CAELON-Bracket-S12l : Black | Thorn-Parts-CAELON-Housing-S12l : Black | TLG_CAEL_F_S12i-S20i-S30i_BK.png | Thorn-Light Sources-CAELON S30i : CAELON S30I 3000-RGBW M BK HL 66 DMX_photometric_data |
| CAELON S30i 3000-RGBW M WH 66 BC | No | Yes | 21035710 | Medium | Thorn CAELON-Accessory-S12i_S20i_S30i : CAELON S COWL/WH | Thorn-Parts-CAELON-Bracket-S12l : White | Thorn-Parts-CAELON-Housing-S12l : White | TLG_CAEL_F_S12i-S20i-S30i_WH.png | Thorn-Light Sources-CAELON S30i : CAELON S30i 3000-RGBW M WH 66 BC_photometric_data |
| CAELON S30I 3000-RGBW M WH 66 DMX | No | Yes | 21035709 | Medium | Thorn CAELON-Accessory-S12i_S20i_S30i : CAELON S COWL/WH | Thorn-Parts-CAELON-Bracket-S12l : White | Thorn-Parts-CAELON-Housing-S12l : White | TLG_CAEL_F_S12i-S20i-S30i_WH.png | Thorn-Light Sources-CAELON S30i : CAELON S30I 3000-RGBW M WH 66 DMX_photometric_data |
| CAELON S30i 3000-RGBW M WH HL 66 BC | No | Yes | 21035707 | Medium | Thorn CAELON-Accessory-S12i_S20i_S30i : CAELON S COWL/WH | Thorn-Parts-CAELON-Bracket-S12l : White | Thorn-Parts-CAELON-Housing-S12l : White | TLG_CAEL_F_S12i-S20i-S30i_WH.png | Thorn-Light Sources-CAELON S30i : CAELON S30i 3000-RGBW M WH HL 66 BC_photometric_data |
| CAELON S30I 3000-RGBW M WH HL 66 DMX | No | Yes | 21035706 | Medium | Thorn CAELON-Accessory-S12i_S20i_S30i : CAELON S COWL/WH | Thorn-Parts-CAELON-Bracket-S12l : White | Thorn-Parts-CAELON-Housing-S12l : White | TLG_CAEL_F_S12i-S20i-S30i_WH.png | Thorn-Light Sources-CAELON S30i : CAELON S30I 3000-RGBW M WH HL 66 DMX_photometric_data |
| CAELON S30i 3000-RGBW N BK 66 BC | Yes | No | 21034404 | Narrow | Thorn CAELON-Accessory-S12i_S20i_S30i : CAELON S COWL/BK | Thorn-Parts-CAELON-Bracket-S12l : Black | Thorn-Parts-CAELON-Housing-S12l : Black | TLG_CAEL_F_S12i-S20i-S30i_BK.png | Thorn-Light Sources-CAELON S30i : CAELON S30i 3000-RGBW N BK 66 BC_photometric_data |
| CAELON S30I 3000-RGBW N BK 66 DMX | Yes | No | 21034403 | Narrow | Thorn CAELON-Accessory-S12i_S20i_S30i : CAELON S COWL/BK | Thorn-Parts-CAELON-Bracket-S12l : Black | Thorn-Parts-CAELON-Housing-S12l : Black | TLG_CAEL_F_S12i-S20i-S30i_BK.png | Thorn-Light Sources-CAELON S30i : CAELON S30I 3000-RGBW N BK 66 DMX_photometric_data |
| CAELON S30i 3000-RGBW N BK HL 66 BC | Yes | No | 21034401 | Narrow | Thorn CAELON-Accessory-S12i_S20i_S30i : CAELON S COWL/BK | Thorn-Parts-CAELON-Bracket-S12l : Black | Thorn-Parts-CAELON-Housing-S12l : Black | TLG_CAEL_F_S12i-S20i-S30i_BK.png | Thorn-Light Sources-CAELON S30i : CAELON S30i 3000-RGBW N BK HL 66 BC_photometric_data |
| CAELON S30I 3000-RGBW N BK HL 66 DMX | Yes | No | 21034400 | Narrow | Thorn CAELON-Accessory-S12i_S20i_S30i : CAELON S COWL/BK | Thorn-Parts-CAELON-Bracket-S12l : Black | Thorn-Parts-CAELON-Housing-S12l : Black | TLG_CAEL_F_S12i-S20i-S30i_BK.png | Thorn-Light Sources-CAELON S30i : CAELON S30I 3000-RGBW N BK HL 66 DMX_photometric_data |
| CAELON S30i 3000-RGBW N WH 66 BC | No | Yes | 21034410 | Narrow | Thorn CAELON-Accessory-S12i_S20i_S30i : CAELON S COWL/WH | Thorn-Parts-CAELON-Bracket-S12l : White | Thorn-Parts-CAELON-Housing-S12l : White | TLG_CAEL_F_S12i-S20i-S30i_WH.png | Thorn-Light Sources-CAELON S30i : CAELON S30i 3000-RGBW N WH 66 BC_photometric_data |
| CAELON S30I 3000-RGBW N WH 66 DMX | No | Yes | 21034409 | Narrow | Thorn CAELON-Accessory-S12i_S20i_S30i : CAELON S COWL/WH | Thorn-Parts-CAELON-Bracket-S12l : White | Thorn-Parts-CAELON-Housing-S12l : White | TLG_CAEL_F_S12i-S20i-S30i_WH.png | Thorn-Light Sources-CAELON S30i : CAELON S30I 3000-RGBW N WH 66 DMX_photometric_data |
| CAELON S30i 3000-RGBW N WH HL 66 BC | No | Yes | 21034407 | Narrow | Thorn CAELON-Accessory-S12i_S20i_S30i : CAELON S COWL/WH | Thorn-Parts-CAELON-Bracket-S12l : White | Thorn-Parts-CAELON-Housing-S12l : White | TLG_CAEL_F_S12i-S20i-S30i_WH.png | Thorn-Light Sources-CAELON S30i : CAELON S30i 3000-RGBW N WH HL 66 BC_photometric_data |
| CAELON S30I 3000-RGBW N WH HL 66 DMX | No | Yes | 21034406 | Narrow | Thorn CAELON-Accessory-S12i_S20i_S30i : CAELON S COWL/WH | Thorn-Parts-CAELON-Bracket-S12l : White | Thorn-Parts-CAELON-Housing-S12l : White | TLG_CAEL_F_S12i-S20i-S30i_WH.png | Thorn-Light Sources-CAELON S30i : CAELON S30I 3000-RGBW N WH HL 66 DMX_photometric_data |
| CAELON S30i 3000-RGBW SN BK 66 BC | Yes | No | 21034392 | Super Narrow | Thorn CAELON-Accessory-S12i_S20i_S30i : CAELON S COWL/BK | Thorn-Parts-CAELON-Bracket-S12l : Black | Thorn-Parts-CAELON-Housing-S12l : Black | TLG_CAEL_F_S12i-S20i-S30i_BK.png | Thorn-Light Sources-CAELON S30i : CAELON S30i 3000-RGBW SN BK 66 BC_photometric_data |
| CAELON S30I 3000-RGBW SN BK 66 DMX | Yes | No | 21034391 | Super Narrow | Thorn CAELON-Accessory-S12i_S20i_S30i : CAELON S COWL/BK | Thorn-Parts-CAELON-Bracket-S12l : Black | Thorn-Parts-CAELON-Housing-S12l : Black | TLG_CAEL_F_S12i-S20i-S30i_BK.png | Thorn-Light Sources-CAELON S30i : CAELON S30I 3000-RGBW SN BK 66 DMX_photometric_data |
| CAELON S30i 3000-RGBW SN BK HL 66 BC | Yes | No | 21034389 | Super Narrow | Thorn CAELON-Accessory-S12i_S20i_S30i : CAELON S COWL/BK | Thorn-Parts-CAELON-Bracket-S12l : Black | Thorn-Parts-CAELON-Housing-S12l : Black | TLG_CAEL_F_S12i-S20i-S30i_BK.png | Thorn-Light Sources-CAELON S30i : CAELON S30i 3000-RGBW SN BK HL 66 BC_photometric_data |
| CAELON S30I 3000-RGBW SN BK HL 66 DMX | Yes | No | 21034388 | Super Narrow | Thorn CAELON-Accessory-S12i_S20i_S30i : CAELON S COWL/BK | Thorn-Parts-CAELON-Bracket-S12l : Black | Thorn-Parts-CAELON-Housing-S12l : Black | TLG_CAEL_F_S12i-S20i-S30i_BK.png | Thorn-Light Sources-CAELON S30i : CAELON S30I 3000-RGBW SN BK HL 66 DMX_photometric_data |
| CAELON S30i 3000-RGBW SN WH 66 BC | No | Yes | 21034398 | Super Narrow | Thorn CAELON-Accessory-S12i_S20i_S30i : CAELON S COWL/WH | Thorn-Parts-CAELON-Bracket-S12l : White | Thorn-Parts-CAELON-Housing-S12l : White | TLG_CAEL_F_S12i-S20i-S30i_WH.png | Thorn-Light Sources-CAELON S30i : CAELON S30i 3000-RGBW SN WH 66 BC_photometric_data |
| CAELON S30I 3000-RGBW SN WH 66 DMX | No | Yes | 21034397 | Super Narrow | Thorn CAELON-Accessory-S12i_S20i_S30i : CAELON S COWL/WH | Thorn-Parts-CAELON-Bracket-S12l : White | Thorn-Parts-CAELON-Housing-S12l : White | TLG_CAEL_F_S12i-S20i-S30i_WH.png | Thorn-Light Sources-CAELON S30i : CAELON S30I 3000-RGBW SN WH 66 DMX_photometric_data |
| CAELON S30i 3000-RGBW SN WH HL 66 BC | No | Yes | 21034395 | Super Narrow | Thorn CAELON-Accessory-S12i_S20i_S30i : CAELON S COWL/WH | Thorn-Parts-CAELON-Bracket-S12l : White | Thorn-Parts-CAELON-Housing-S12l : White | TLG_CAEL_F_S12i-S20i-S30i_WH.png | Thorn-Light Sources-CAELON S30i : CAELON S30i 3000-RGBW SN WH HL 66 BC_photometric_data |
| CAELON S30I 3000-RGBW SN WH HL 66 DMX | No | Yes | 21034394 | Super Narrow | Thorn CAELON-Accessory-S12i_S20i_S30i : CAELON S COWL/WH | Thorn-Parts-CAELON-Bracket-S12l : White | Thorn-Parts-CAELON-Housing-S12l : White | TLG_CAEL_F_S12i-S20i-S30i_WH.png | Thorn-Light Sources-CAELON S30i : CAELON S30I 3000-RGBW SN WH HL 66 DMX_photometric_data |
| CAELON S30i 3000-RGBW W BK 66 BC | Yes | No | 21034413 | Wide | Thorn CAELON-Accessory-S12i_S20i_S30i : CAELON S COWL/BK | Thorn-Parts-CAELON-Bracket-S12l : Black | Thorn-Parts-CAELON-Housing-S12l : Black | TLG_CAEL_F_S12i-S20i-S30i_BK.png | Thorn-Light Sources-CAELON S30i : CAELON S30i 3000-RGBW W BK 66 BC_photometric_data |
| CAELON S30I 3000-RGBW W BK 66 DMX | Yes | No | 21034412 | Wide | Thorn CAELON-Accessory-S12i_S20i_S30i : CAELON S COWL/BK | Thorn-Parts-CAELON-Bracket-S12l : Black | Thorn-Parts-CAELON-Housing-S12l : Black | TLG_CAEL_F_S12i-S20i-S30i_BK.png | Thorn-Light Sources-CAELON S30i : CAELON S30I 3000-RGBW W BK 66 DMX_photometric_data |
| CAELON S30i 3000-RGBW W WH 66 BC | No | Yes | 21034416 | Wide | Thorn CAELON-Accessory-S12i_S20i_S30i : CAELON S COWL/WH | Thorn-Parts-CAELON-Bracket-S12l : White | Thorn-Parts-CAELON-Housing-S12l : White | TLG_CAEL_F_S12i-S20i-S30i_WH.png | Thorn-Light Sources-CAELON S30i : CAELON S30i 3000-RGBW W WH 66 BC_photometric_data |
| CAELON S30I 3000-RGBW W WH 66 DMX | No | Yes | 21034415 | Wide | Thorn CAELON-Accessory-S12i_S20i_S30i : CAELON S COWL/WH | Thorn-Parts-CAELON-Bracket-S12l : White | Thorn-Parts-CAELON-Housing-S12l : White | TLG_CAEL_F_S12i-S20i-S30i_WH.png | Thorn-Light Sources-CAELON S30i : CAELON S30I 3000-RGBW W WH 66 DMX_photometric_data |

note: [stored X ft] marks values corroborated as IEEE doubles in the binary element streams (Revit-internal decimal feet)

## geometry (parser evidence)
native form markers: Sweep x10
no freeform markers — native parametric forms only
